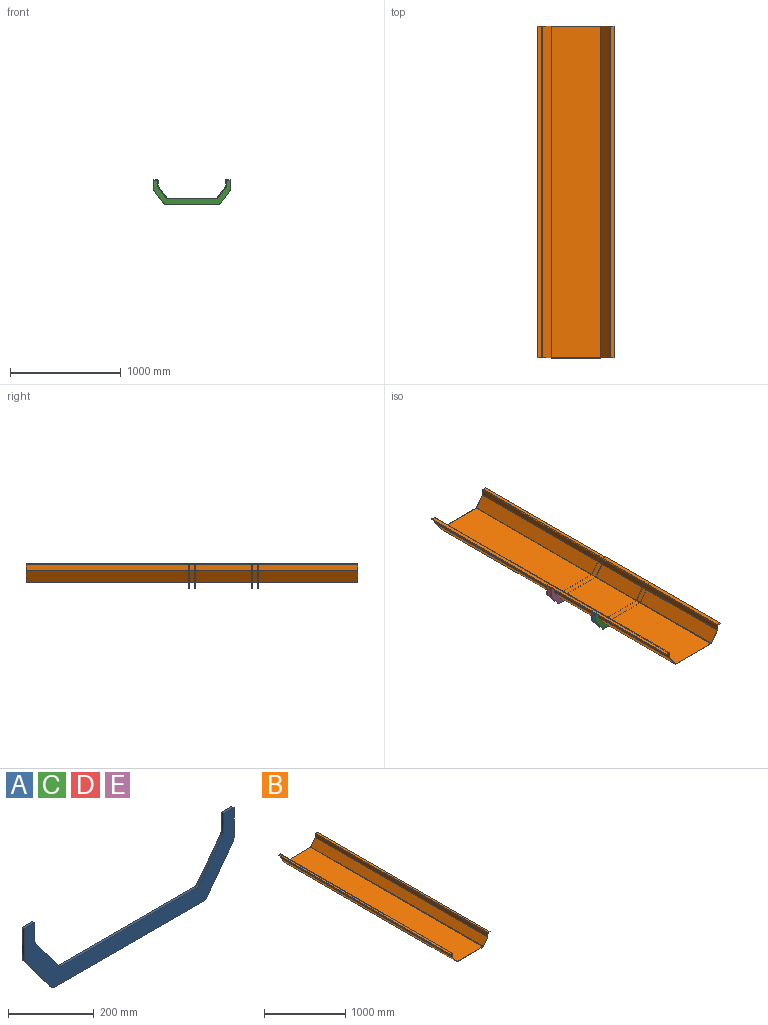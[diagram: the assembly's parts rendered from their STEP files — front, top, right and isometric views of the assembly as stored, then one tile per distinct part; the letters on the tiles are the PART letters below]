
ASSEMBLY  parts=5 mates=4
PART A: 22 faces, bbox 690x8x216 mm
  f0: cylinder r=20mm len=11.97mm, axis (0,1,0), area 102.7mm2, adj f1,f19,f20,f21
  f1: plane 50.33x8mm, normal (1,0,0), area 402.6mm2, adj f0,f2,f20,f21
  f2: plane 34x8mm, normal (0,0,1), area 272mm2, adj f1,f3,f20,f21
  f3: plane 85.01x8mm, normal (-1,0,0), area 680.1mm2, adj f2,f4,f20,f21
  f4: cylinder r=20mm len=11.97mm, axis (0,1,0), area 102.7mm2, adj f3,f5,f20,f21
  f5: plane 115x85.97mm, normal (-0.8,0,-0.6), area 1148.6mm2, adj f4,f6,f20,f21
  f6: cylinder r=10mm len=8.01mm, axis (0,1,0), area 74.3mm2, adj f5,f7,f20,f21
  f7: plane 494.09x8mm, normal (0,0,-1), area 3952.7mm2, adj f6,f8,f20,f21
  f8: cylinder r=10mm len=8.01mm, axis (0,1,0), area 74.3mm2, adj f7,f9,f20,f21
  f9: plane 115x85.97mm, normal (0.8,0,-0.6), area 1148.6mm2, adj f8,f10,f20,f21
  f10: cylinder r=20mm len=11.97mm, axis (0,1,0), area 102.7mm2, adj f9,f11,f20,f21
  f11: plane 85.01x8mm, normal (1,0,0), area 680.1mm2, adj f10,f12,f20,f21
  f12: plane 34x8mm, normal (0,0,1), area 272mm2, adj f11,f13,f20,f21
  f13: plane 50.33x8mm, normal (-1,0,0), area 402.6mm2, adj f12,f14,f20,f21
  f14: cylinder r=20mm len=11.97mm, axis (0,1,0), area 102.7mm2, adj f13,f15,f20,f21
  f15: plane 101.68x76.01mm, normal (-0.8,0,0.6), area 1015.6mm2, adj f14,f16,f20,f21
  f16: cylinder r=10mm len=8.01mm, axis (0,1,0), area 74.3mm2, adj f15,f17,f20,f21
  f17: plane 445.99x8mm, normal (0,0,1), area 3567.9mm2, adj f16,f18,f20,f21
  f18: cylinder r=10mm len=8.01mm, axis (0,1,0), area 74.3mm2, adj f17,f19,f20,f21
  f19: plane 101.68x76.01mm, normal (0.8,0,0.6), area 1015.6mm2, adj f0,f18,f20,f21
  f20: plane 690x216mm, normal (0,-1,0), area 42201.5mm2, adj f0,f1,f2,f3,f4,f5,f6,f7
  f21: plane 690x216mm, normal (0,1,0), area 42201.5mm2, adj f0,f1,f2,f3,f4,f5,f6,f7
PART B: 30 faces, bbox 690x3000x170 mm
  f0: plane 3000x35mm, normal (0,0,1), area 105000mm2, adj f1,f16,f17,f29
  f1: plane 3000x4mm, normal (-1,0,0), area 12000mm2, adj f0,f2,f16,f17
  f2: plane 3000x31mm, normal (0,0,-1), area 93000mm2, adj f1,f16,f17,f19
  f3: plane 3000x49.65mm, normal (-1,0,0), area 148949.8mm2, adj f16,f17,f19,f20
  f4: plane 3000x106.35mm, normal (-0.8,0,-0.6), area 398342.4mm2, adj f16,f17,f20,f21
  f5: plane 3000x449mm, normal (0,0,-1), area 1346994.1mm2, adj f16,f17,f21,f22
  f6: plane 3000x106.35mm, normal (0.8,0,-0.6), area 398342.4mm2, adj f16,f17,f18,f22
  f7: plane 3000x50.65mm, normal (1,0,0), area 151949.8mm2, adj f16,f17,f18,f23
  f8: plane 3000x31mm, normal (0,0,-1), area 93000mm2, adj f9,f16,f17,f23
  f9: plane 3000x3mm, normal (1,0,0), area 9000mm2, adj f8,f10,f16,f17
  f10: plane 3000x35mm, normal (0,0,1), area 105000mm2, adj f9,f16,f17,f24
  f11: plane 3000x52.32mm, normal (-1,0,0), area 156960.3mm2, adj f16,f17,f24,f25
  f12: plane 3000x103.68mm, normal (-0.8,0,0.6), area 388341.1mm2, adj f16,f17,f25,f26
  f13: plane 3000x444.99mm, normal (0,0,1), area 1334970.4mm2, adj f16,f17,f26,f27
  f14: plane 3000x103.68mm, normal (0.8,0,0.6), area 388341.1mm2, adj f16,f17,f27,f28
  f15: plane 3000x52.32mm, normal (1,0,0), area 156960.3mm2, adj f16,f17,f28,f29
  f16: plane 690x170mm, normal (0,-1,0), area 3619.4mm2, adj f0,f1,f2,f3,f4,f5,f6,f7
  f17: plane 690x170mm, normal (0,1,0), area 3619.4mm2, adj f0,f1,f2,f3,f4,f5,f6,f7
  f18: cylinder r=5mm len=3000mm, axis (0,1,0), area 9628.9mm2, adj f6,f7,f16,f17
  f19: cylinder r=5mm len=3000mm, axis (0,1,0), area 23561.9mm2, adj f2,f3,f16,f17
  f20: cylinder r=5mm len=3000mm, axis (0,1,0), area 9628.9mm2, adj f3,f4,f16,f17
  f21: cylinder r=5mm len=3000mm, axis (0,1,0), area 13933.1mm2, adj f4,f5,f16,f17
  f22: cylinder r=5mm len=3000mm, axis (0,-1,0), area 13933.1mm2, adj f5,f6,f16,f17
  f23: cylinder r=5mm len=3000mm, axis (0,1,0), area 23561.9mm2, adj f7,f8,f16,f17
  f24: cylinder r=5mm len=3000mm, axis (0,1,0), area 23561.9mm2, adj f10,f11,f16,f17
  f25: cylinder r=5mm len=3000mm, axis (0,-1,0), area 9628.9mm2, adj f11,f12,f16,f17
  f26: cylinder r=5mm len=3000mm, axis (0,1,0), area 13933.1mm2, adj f12,f13,f16,f17
  f27: cylinder r=5mm len=3000mm, axis (0,-1,0), area 13933.1mm2, adj f13,f14,f16,f17
  f28: cylinder r=5mm len=3000mm, axis (0,-1,0), area 9628.9mm2, adj f14,f15,f16,f17
  f29: cylinder r=5mm len=3000mm, axis (0,1,0), area 23561.9mm2, adj f0,f15,f16,f17
PART C: same geometry as A
PART D: same geometry as A
PART E: same geometry as A
PLACE A t=(-1769.7,-2878.02,-1419.33)mm
PLACE B t=(-1769.7,-836.02,-1392.33)mm
PLACE C t=(-1768.7,-2926.02,-1419.33)mm
PLACE D t=(-1769.7,-2304.02,-1419.33)mm
PLACE E t=(-1768.7,-2358.02,-1419.33)mm
MATE planar C.f2 <-> B.f2  axis (0,0,1) through (-2096.7,-2930.02,-1311.33)mm
MATE planar D.f2 <-> B.f2  axis (0,0,1) through (-2114.7,-2304.02,-1311.33)mm
MATE planar A.f2 <-> B.f2  axis (0,0,1) through (-2097.7,-2878.02,-1311.33)mm
MATE planar E.f2 <-> B.f2  axis (0,0,1) through (-2096.7,-2362.02,-1311.33)mm
